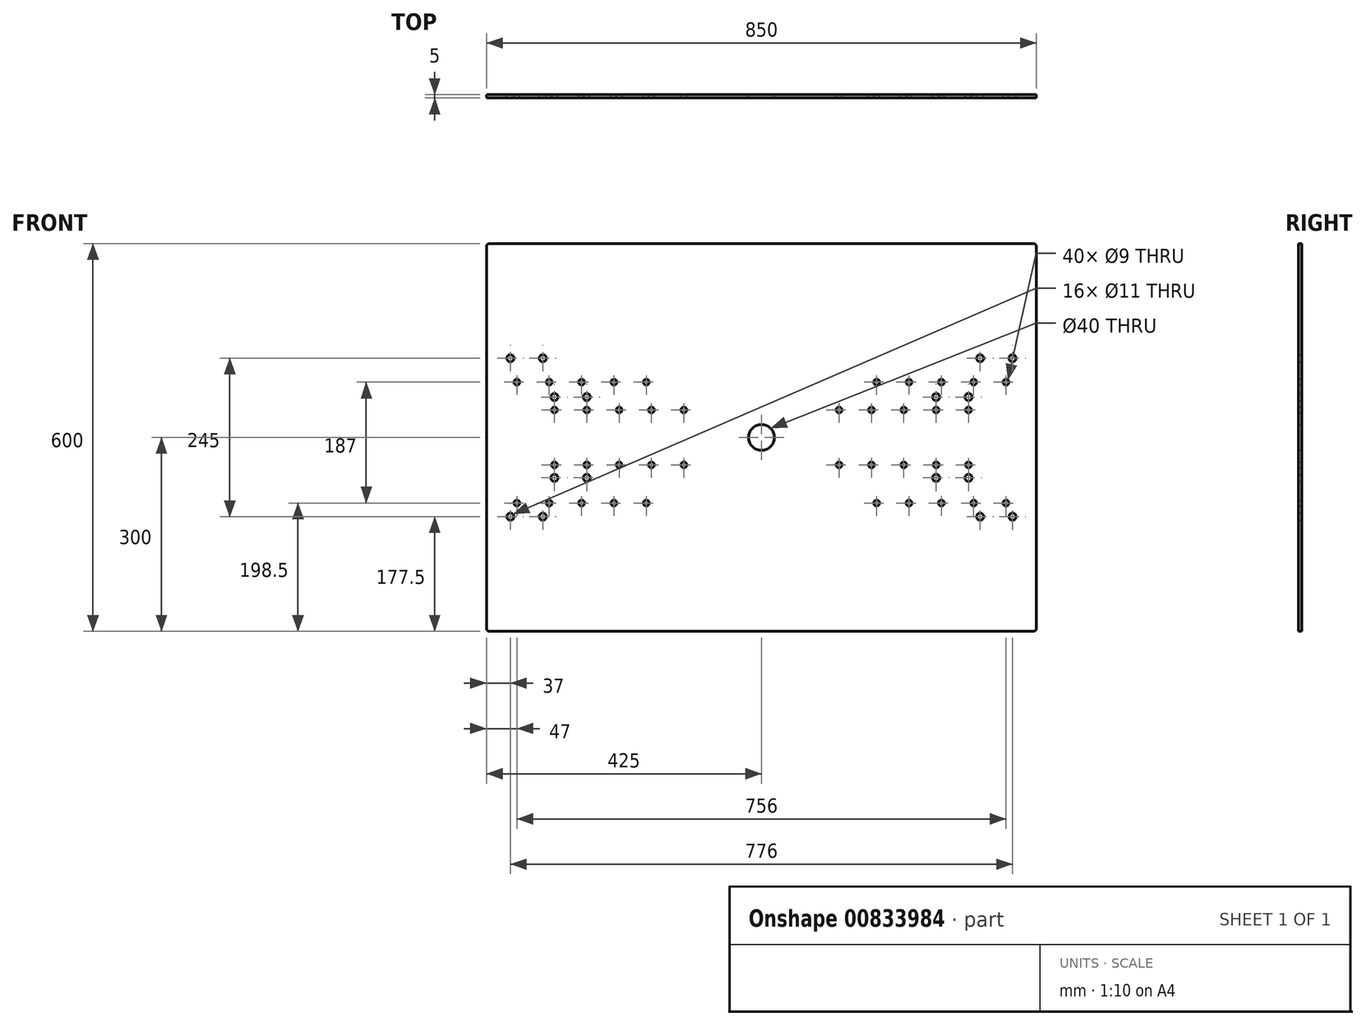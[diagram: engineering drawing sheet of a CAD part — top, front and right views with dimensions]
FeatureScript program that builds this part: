
annotation { "Feature Type Name" : "Feature", "Feature Type Description" : "" }
export const myFeature = defineFeature(function(context is Context, id is Id, definition is map)
    precondition{}
    {
        {
            var Q0;
            Q0=qCreatedBy(makeId("Front.planeOp"),FACE);
            var sketch = newSketch(context, id + "F0", { "sketchPlane" : qUnion([Q0])});
            skLineSegment(sketch, "E0.bottom", {"start": v(425, 300) * mm, "end": v(-425, 300) * mm});
            skLineSegment(sketch, "E0.top", {"start": v(425, -300) * mm, "end": v(-425, -300) * mm});
            skLineSegment(sketch, "E0.left", {"start": v(425, 300) * mm, "end": v(425, -300) * mm});
            skLineSegment(sketch, "E0.right", {"start": v(-425, 300) * mm, "end": v(-425, -300) * mm});
            skPoint(sketch, "E0.middle", {"position": v(0, 0) * mm});
            skLineSegment(sketch, "E1", {"start": v(-425, 0) * mm, "end": v(425, 0) * mm, "construction": true});
            skLineSegment(sketch, "E2", {"start": v(0, -165.8) * mm, "end": v(0, 149.61) * mm, "construction": true});
            skLineSegment(sketch, "E3.MirrorCS", {"start": v(120, 112.6) * mm, "end": v(120, -109.12) * mm, "construction": true});
            skCircle(sketch, "E4", {"center": v(120, 42.5) * mm, "radius": 4.5 * mm});
            skCircle(sketch, "E5", {"center": v(120, -42.5) * mm, "radius": 4.5 * mm});
            skCircle(sketch, "E6.1.0.0", {"center": v(170, -42.5) * mm, "radius": 4.5 * mm});
            skCircle(sketch, "E6.1.0.1", {"center": v(170, 42.5) * mm, "radius": 4.5 * mm});
            skCircle(sketch, "E6.2.0.0", {"center": v(220, -42.5) * mm, "radius": 4.5 * mm});
            skCircle(sketch, "E6.2.0.1", {"center": v(220, 42.5) * mm, "radius": 4.5 * mm});
            skCircle(sketch, "E6.3.0.0", {"center": v(270, -42.5) * mm, "radius": 4.5 * mm});
            skCircle(sketch, "E6.3.0.1", {"center": v(270, 42.5) * mm, "radius": 4.5 * mm});
            skCircle(sketch, "E6.4.0.0", {"center": v(320, -42.5) * mm, "radius": 4.5 * mm});
            skCircle(sketch, "E6.4.0.1", {"center": v(320, 42.5) * mm, "radius": 4.5 * mm});
            skLineSegment(sketch, "E6.direction1", {"start": v(120, -42.5) * mm, "end": v(170, -42.5) * mm, "construction": true});
            skCircle(sketch, "E7", {"center": v(178, 85.5) * mm, "radius": 4.5 * mm});
            skCircle(sketch, "E8", {"center": v(178, -101.5) * mm, "radius": 4.5 * mm});
            skCircle(sketch, "E9.1.0.0", {"center": v(228, -101.5) * mm, "radius": 4.5 * mm});
            skCircle(sketch, "E9.1.0.1", {"center": v(228, 85.5) * mm, "radius": 4.5 * mm});
            skCircle(sketch, "E9.2.0.0", {"center": v(278, -101.5) * mm, "radius": 4.5 * mm});
            skCircle(sketch, "E9.2.0.1", {"center": v(278, 85.5) * mm, "radius": 4.5 * mm});
            skCircle(sketch, "E9.3.0.0", {"center": v(328, -101.5) * mm, "radius": 4.5 * mm});
            skCircle(sketch, "E9.3.0.1", {"center": v(328, 85.5) * mm, "radius": 4.5 * mm});
            skCircle(sketch, "E9.4.0.0", {"center": v(378, -101.5) * mm, "radius": 4.5 * mm});
            skCircle(sketch, "E9.4.0.1", {"center": v(378, 85.5) * mm, "radius": 4.5 * mm});
            skLineSegment(sketch, "E9.direction1", {"start": v(178, -101.5) * mm, "end": v(228, -101.5) * mm, "construction": true});
            skCircle(sketch, "E10", {"center": v(270, 62.5) * mm, "radius": 5.5 * mm});
            skCircle(sketch, "E11.0.1.0", {"center": v(270, -62.5) * mm, "radius": 5.5 * mm});
            skCircle(sketch, "E11.1.0.0", {"center": v(320, 62.5) * mm, "radius": 5.5 * mm});
            skCircle(sketch, "E11.1.1.0", {"center": v(320, -62.5) * mm, "radius": 5.5 * mm});
            skLineSegment(sketch, "E11.direction1", {"start": v(270, 62.5) * mm, "end": v(320, 62.5) * mm, "construction": true});
            skLineSegment(sketch, "E11.direction2", {"start": v(270, 62.5) * mm, "end": v(270, -62.5) * mm, "construction": true});
            skCircle(sketch, "E12", {"center": v(338, 122.5) * mm, "radius": 5.5 * mm});
            skCircle(sketch, "E13.0.1.0", {"center": v(338, -122.5) * mm, "radius": 5.5 * mm});
            skCircle(sketch, "E13.1.0.0", {"center": v(388, 122.5) * mm, "radius": 5.5 * mm});
            skCircle(sketch, "E13.1.1.0", {"center": v(388, -122.5) * mm, "radius": 5.5 * mm});
            skLineSegment(sketch, "E13.direction1", {"start": v(338, 122.5) * mm, "end": v(388, 122.5) * mm, "construction": true});
            skLineSegment(sketch, "E13.direction2", {"start": v(338, 122.5) * mm, "end": v(338, -122.5) * mm, "construction": true});
            skCircle(sketch, "E14.MirrorC", {"center": v(-270, 62.5) * mm, "radius": 5.5 * mm});
            skCircle(sketch, "E15.MirrorC", {"center": v(-338, 122.5) * mm, "radius": 5.5 * mm});
            skCircle(sketch, "E16.MirrorC", {"center": v(-228, -101.5) * mm, "radius": 4.5 * mm});
            skCircle(sketch, "E17.MirrorC", {"center": v(-120, -42.5) * mm, "radius": 4.5 * mm});
            skCircle(sketch, "E18.MirrorC", {"center": v(-320, 62.5) * mm, "radius": 5.5 * mm});
            skCircle(sketch, "E19.MirrorC", {"center": v(-338, -122.5) * mm, "radius": 5.5 * mm});
            skCircle(sketch, "E20.MirrorC", {"center": v(-178, -101.5) * mm, "radius": 4.5 * mm});
            skCircle(sketch, "E21.MirrorC", {"center": v(-388, 122.5) * mm, "radius": 5.5 * mm});
            skCircle(sketch, "E22.MirrorC", {"center": v(-170, -42.5) * mm, "radius": 4.5 * mm});
            skCircle(sketch, "E23.MirrorC", {"center": v(-270, -62.5) * mm, "radius": 5.5 * mm});
            skCircle(sketch, "E24.MirrorC", {"center": v(-328, -101.5) * mm, "radius": 4.5 * mm});
            skCircle(sketch, "E25.MirrorC", {"center": v(-378, -101.5) * mm, "radius": 4.5 * mm});
            skCircle(sketch, "E26.MirrorC", {"center": v(-270, -42.5) * mm, "radius": 4.5 * mm});
            skCircle(sketch, "E27.MirrorC", {"center": v(-278, 85.5) * mm, "radius": 4.5 * mm});
            skCircle(sketch, "E28.MirrorC", {"center": v(-378, 85.5) * mm, "radius": 4.5 * mm});
            skCircle(sketch, "E29.MirrorC", {"center": v(-178, 85.5) * mm, "radius": 4.5 * mm});
            skCircle(sketch, "E30.MirrorC", {"center": v(-328, 85.5) * mm, "radius": 4.5 * mm});
            skCircle(sketch, "E31.MirrorC", {"center": v(-120, 42.5) * mm, "radius": 4.5 * mm});
            skCircle(sketch, "E32.MirrorC", {"center": v(-320, -42.5) * mm, "radius": 4.5 * mm});
            skCircle(sketch, "E33.MirrorC", {"center": v(-228, 85.5) * mm, "radius": 4.5 * mm});
            skCircle(sketch, "E34.MirrorC", {"center": v(-220, 42.5) * mm, "radius": 4.5 * mm});
            skCircle(sketch, "E35.MirrorC", {"center": v(-270, 42.5) * mm, "radius": 4.5 * mm});
            skCircle(sketch, "E36.MirrorC", {"center": v(-320, 42.5) * mm, "radius": 4.5 * mm});
            skCircle(sketch, "E37.MirrorC", {"center": v(-220, -42.5) * mm, "radius": 4.5 * mm});
            skLineSegment(sketch, "E38.MirrorCS", {"start": v(-270, 62.5) * mm, "end": v(-320, 62.5) * mm, "construction": true});
            skCircle(sketch, "E39.MirrorC", {"center": v(-170, 42.5) * mm, "radius": 4.5 * mm});
            skCircle(sketch, "E40.MirrorC", {"center": v(-320, -62.5) * mm, "radius": 5.5 * mm});
            skLineSegment(sketch, "E41.MirrorCS", {"start": v(-178, -101.5) * mm, "end": v(-228, -101.5) * mm, "construction": true});
            skCircle(sketch, "E42.MirrorC", {"center": v(-388, -122.5) * mm, "radius": 5.5 * mm});
            skCircle(sketch, "E43.MirrorC", {"center": v(-278, -101.5) * mm, "radius": 4.5 * mm});
            skLineSegment(sketch, "E44.MirrorCS", {"start": v(-270, 62.5) * mm, "end": v(-270, -62.5) * mm, "construction": true});
            skLineSegment(sketch, "E45.MirrorCS", {"start": v(-338, 122.5) * mm, "end": v(-338, -122.5) * mm, "construction": true});
            skLineSegment(sketch, "E46.MirrorCS", {"start": v(-338, 122.5) * mm, "end": v(-388, 122.5) * mm, "construction": true});
            skLineSegment(sketch, "E47.MirrorCS", {"start": v(-120, 112.6) * mm, "end": v(-120, -109.12) * mm, "construction": true});
            skLineSegment(sketch, "E48.MirrorCS", {"start": v(-120, -42.5) * mm, "end": v(-170, -42.5) * mm, "construction": true});
            skCircle(sketch, "E49", {"center": v(0, 0) * mm, "radius": 20 * mm});
            skSolve(sketch);
        }
        {
            var Q0;
            Q0=makeQuery(id+"F0.imprint","IMPRINT",FACE,{"disambiguationData":[TD([[makeQuery(id+"F0.imprint","IMPRINT",EDGE,{"derivedFrom":sQuery(id+"F0.wireOp",EDGE,"E0.bottom")}),1.0]])]});
            extrude(context, id + "F1", {"entities" : qUnion([Q0]), "depth" : 5 * mm, "offsetDistance" : 25 * mm});
        }
        {
            var Q0;
            Q0=makeQuery(id+"F1.opExtrude","SWEPT_EDGE",EDGE,{"disambiguationData":[OSD([sQuery(id+"F0.wireOp",EDGE,"E0.bottom"),sQuery(id+"F0.wireOp",EDGE,"E0.right")])]});
            var Q1;
            Q1=makeQuery(id+"F1.opExtrude","SWEPT_EDGE",EDGE,{"disambiguationData":[OSD([sQuery(id+"F0.wireOp",EDGE,"E0.bottom"),sQuery(id+"F0.wireOp",EDGE,"E0.left")])]});
            var Q2;
            Q2=makeQuery(id+"F1.opExtrude","SWEPT_EDGE",EDGE,{"disambiguationData":[OSD([sQuery(id+"F0.wireOp",EDGE,"E0.top"),sQuery(id+"F0.wireOp",EDGE,"E0.left")])]});
            var Q3;
            Q3=makeQuery(id+"F1.opExtrude","SWEPT_EDGE",EDGE,{"disambiguationData":[OSD([sQuery(id+"F0.wireOp",EDGE,"E0.top"),sQuery(id+"F0.wireOp",EDGE,"E0.right")])]});
            fillet(context, id + "F2", {"entities" : qUnion([Q0, Q1, Q2, Q3]), "radius" : 5 * mm, "tangentPropagation" : true, "allowEdgeOverflow" : false});
        }
    });
